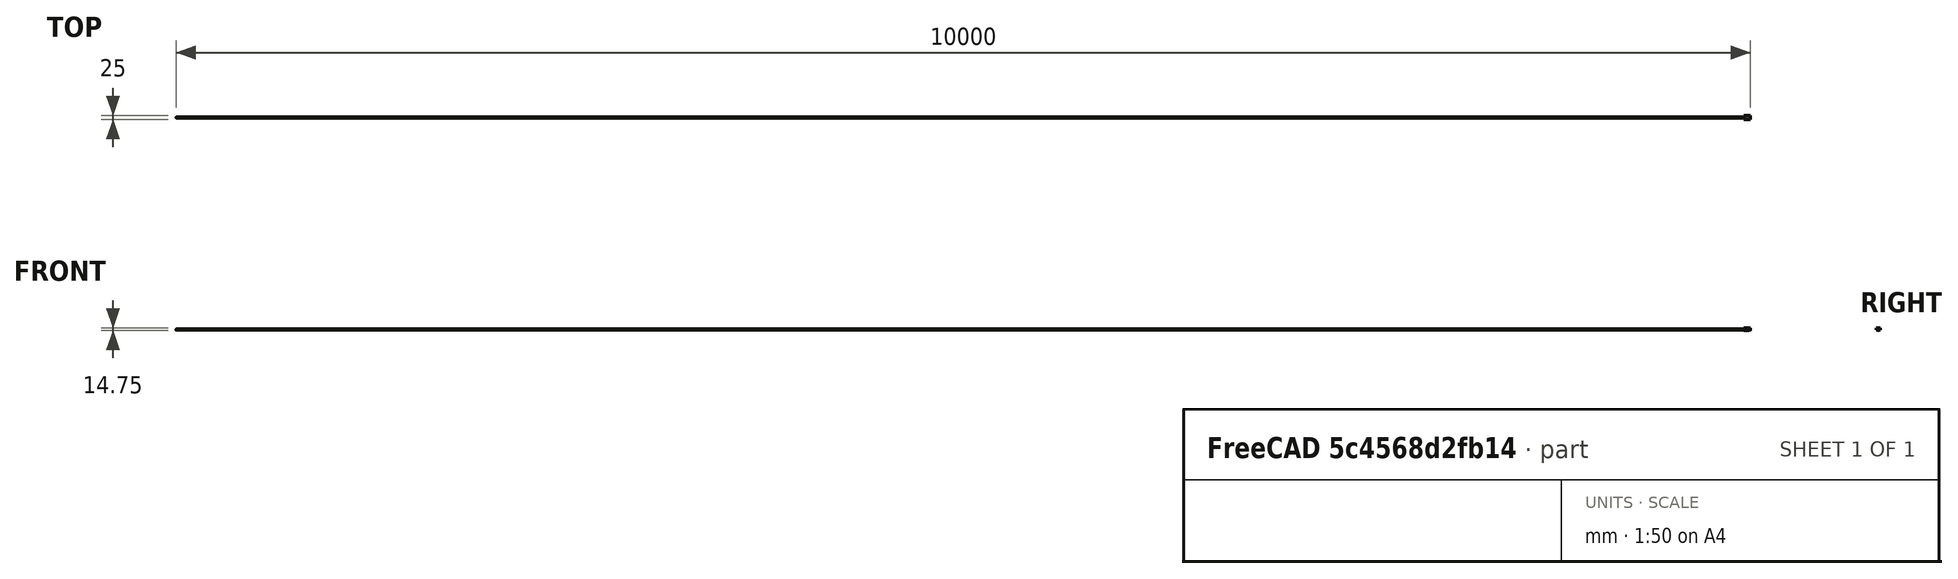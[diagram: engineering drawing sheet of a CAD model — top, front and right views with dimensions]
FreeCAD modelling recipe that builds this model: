
FCSTD DOCUMENT  (FreeCAD 0.16R)
Label: MazdaClip2
License: All rights reserved
LicenseURL: http://en.wikipedia.org/wiki/All_rights_reserved
objects: Sketcher::SketchObject×4, PartDesign::Pocket×3, PartDesign::Fillet×3, PartDesign::Pad×1, PartDesign::Chamfer×1, Mesh::Feature×1
note: 16 computed .brp shape members not serialized (recipe doc carries the construction recipe); baked Part::Feature solids carry a one-line shape summary decoded from their .brp

FEATURE [Sketcher::SketchObject] Sketch
  sketch-geometry (4):
    g0: LineSegment StartX=-20 StartY=12.5 StartZ=0 EndX=20 EndY=12.5 EndZ=0
    g1: LineSegment StartX=20 StartY=12.5 StartZ=0 EndX=20 EndY=-12.5 EndZ=0
    g2: LineSegment StartX=20 StartY=-12.5 StartZ=0 EndX=-20 EndY=-12.5 EndZ=0
    g3: LineSegment StartX=-20 StartY=-12.5 StartZ=0 EndX=-20 EndY=12.5 EndZ=0
  constraints (11):
    c: Coincident(g0,g1)
    c: Coincident(g1,g2)
    c: Coincident(g2,g3)
    c: Coincident(g3,g0)
    c: Horizontal(g0)
    c: Horizontal(g2)
    c: Vertical(g1)
    c: Vertical(g3)
    c: Symmetric(g1,g0,g-1)
    c: Distance(g1) = 25
    c: Distance(g0) = 40
FEATURE [PartDesign::Pad] Pad
  Length = 11
  Length2 = 100
  Sketch = -> Sketch
  Type = 0
FEATURE [Sketcher::SketchObject] Sketch001
  Placement = pos=(20,0,0) rot=(0.57735,0.57735,0.57735;2.0944rad)
  Support = -> Pad [Face2]
  sketch-geometry (1):
    g0: Circle CenterX=0 CenterY=1.25 CenterZ=0 NormalX=0 NormalY=0 NormalZ=1 Radius=2.5
  constraints (3):
    c: PointOnObject(g0,g-2)
    c: Radius(g0) = 2.5
    c: DistanceY(g0) = 1.25
FEATURE [PartDesign::Pocket] Pocket
  Length = 5
  Sketch = -> Sketch001
  Type = 1
FEATURE [Sketcher::SketchObject] Sketch002
  ExternalGeometry = -> [Pocket]
  Placement = pos=(-20,0,0) rot=(0.57735,-0.57735,-0.57735;2.0944rad)
  Support = -> Pocket [Face2]
  sketch-geometry (1):
    g0: Circle CenterX=0 CenterY=1.25 CenterZ=0 NormalX=0 NormalY=0 NormalZ=1 Radius=5
  constraints (3):
    c: Radius(g0) = 5
    c: PointOnObject(g0,g-2)
    c: Coincident(g0,g-3)
FEATURE [PartDesign::Pocket] Pocket001
  Length = 30
  Sketch = -> Sketch002
  Type = 0
FEATURE [Sketcher::SketchObject] Sketch003
  ExternalGeometry = -> [Pocket001]
  Placement = pos=(0,0,0) rot=(1,0,0;3.14159rad)
  Support = -> Pocket001 [Face6]
  sketch-geometry (4):
    g0: LineSegment StartX=-7.21427 StartY=16.2213 StartZ=0 EndX=-15.5 EndY=16.2213 EndZ=0
    g1: LineSegment StartX=-15.5 StartY=16.2213 StartZ=0 EndX=-15.5 EndY=-15.7294 EndZ=0
    g2: LineSegment StartX=-15.5 StartY=-15.7294 StartZ=0 EndX=-7.21427 EndY=-15.7294 EndZ=0
    g3: LineSegment StartX=-7.21427 StartY=-15.7294 StartZ=0 EndX=-7.21427 EndY=16.2213 EndZ=0
  constraints (9):
    c: Coincident(g0,g1)
    c: Coincident(g1,g2)
    c: Coincident(g2,g3)
    c: Coincident(g3,g0)
    c: Horizontal(g0)
    c: Horizontal(g2)
    c: Vertical(g1)
    c: Vertical(g3)
    c: Distance(g-3,g1) = 25.5
FEATURE [PartDesign::Pocket] Pocket002
  Length = 8
  Sketch = -> Sketch003
  Type = 0
FEATURE [PartDesign::Fillet] Fillet
  Base = -> Pocket002 [Edge6,Edge8,Edge38,Edge31,Edge23,Edge16,Edge4,Edge2]
  Radius = 1
FEATURE [PartDesign::Fillet] Fillet001
  Base = -> Fillet [Edge64,Edge47]
  Radius = 1
FEATURE [PartDesign::Fillet] Fillet002
  Base = -> Fillet001 [Edge73]
  Radius = 1
FEATURE [PartDesign::Chamfer] Chamfer
  Base = -> Fillet002 [Edge34,Edge54,Edge28,Edge55,Edge22,Edge56,Edge57,Edge58]
  Size = 1
FEATURE [Mesh::Feature] Mesh  label="Chamfer (Meshed)"
